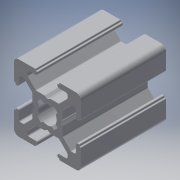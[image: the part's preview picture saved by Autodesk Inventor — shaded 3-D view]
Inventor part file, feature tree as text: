
AUTODESK INVENTOR PART (.ipt)
format: ipt  version: 2019 (Build 230136000, 136)  size: 323,584 bytes
history: native  units: in
note: dims shown in document units (in); Inventor stores cm internally (conversion verified against a paired STEP export)
features: other x3, extrude x1, sketch x1
ambient origin geometry x8: Origin, YZ Plane, XZ Plane, XY Plane, X Axis, Y Axis, Z Axis, Center Point
bodies: Solid1 (feature_tree)
feature tree (5):
  other  "Blocks"
  extrude  "Extrusion1"  Depth=1.0in
  sketch  "Sketch1"  dims[d1=0.0in d13=1.0in d14=1.0in]
  other  "20x20"
  other  "20x20:1"
